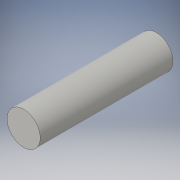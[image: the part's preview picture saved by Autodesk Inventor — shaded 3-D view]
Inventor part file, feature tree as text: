
AUTODESK INVENTOR PART (.ipt)
format: ipt  version: 2016 (Build 200138000, 138)  size: 86,016 bytes
history: native  units: in
note: dims shown in document units (in); Inventor stores cm internally (conversion verified against a paired STEP export)
features: extrude x1, sketch x1
ambient origin geometry x8: Origin, YZ Plane, XZ Plane, XY Plane, X Axis, Y Axis, Z Axis, Center Point
bodies: Solid1 (feature_tree)
feature tree (2):
  extrude  "Extrusion1"  Depth=3.0in TaperAngle=0.0deg
  sketch  "Sketch1"  dims[d0=0.75in d1=3.0in d2=0.0in]
